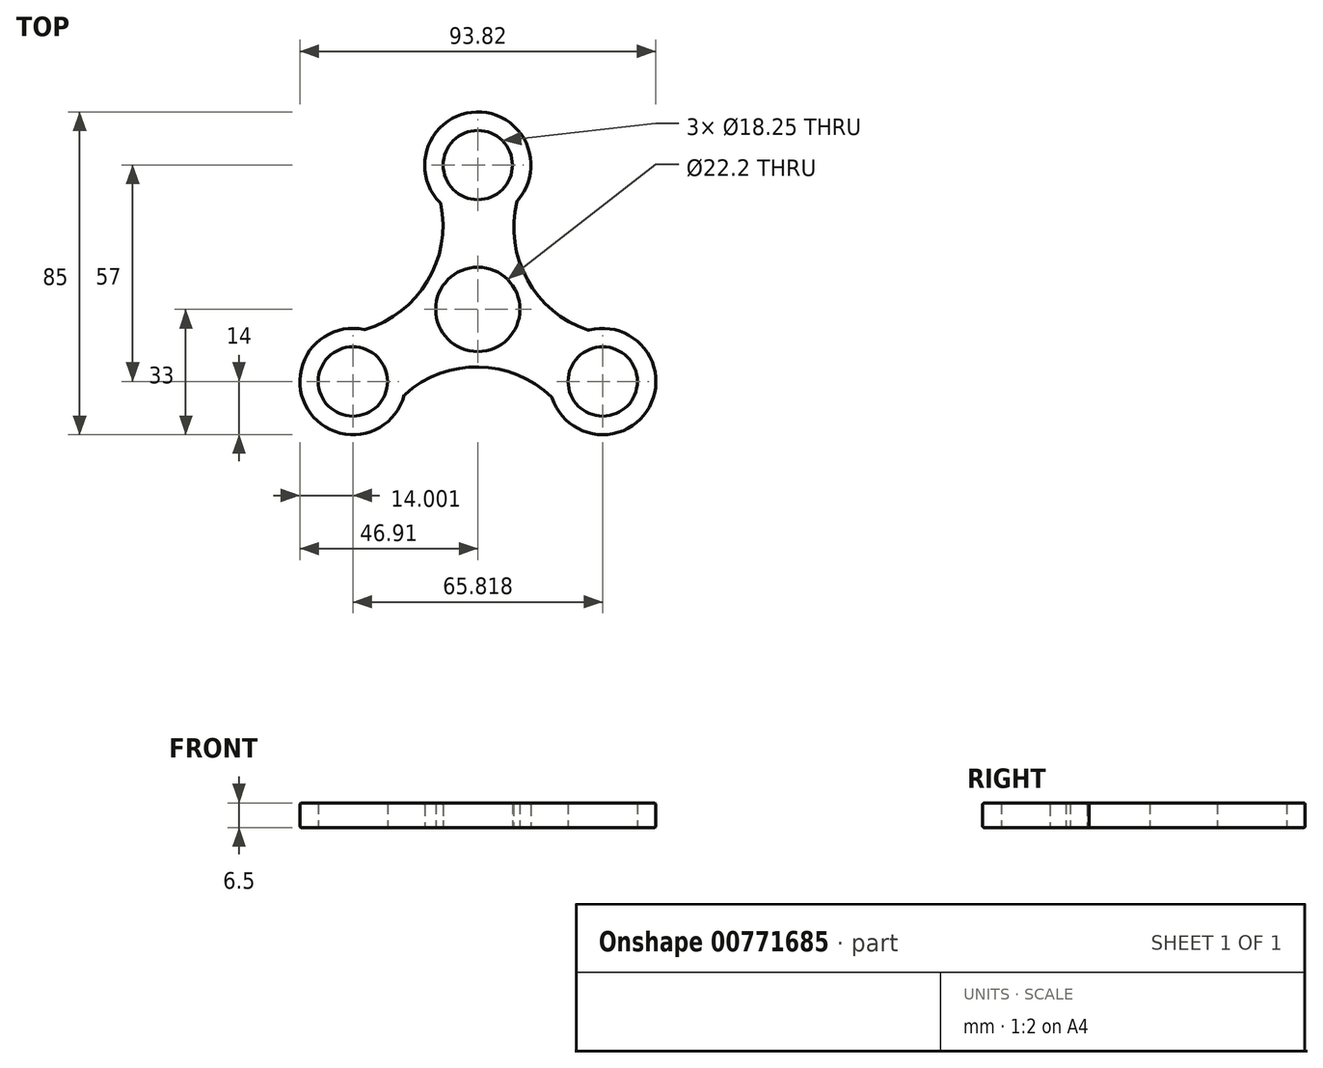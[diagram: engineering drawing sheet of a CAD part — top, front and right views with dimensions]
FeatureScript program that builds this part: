
annotation { "Feature Type Name" : "Feature", "Feature Type Description" : "" }
export const myFeature = defineFeature(function(context is Context, id is Id, definition is map)
    precondition{}
    {
        {
            var Q0;
            Q0=qCreatedBy(makeId("Top.planeOp"),FACE);
            var sketch = newSketch(context, id + "F0", { "sketchPlane" : qUnion([Q0])});
            skCircle(sketch, "E0", {"center": v(0, 0) * mm, "radius": 11.1 * mm});
            skCircle(sketch, "E1", {"center": v(0, 0) * mm, "radius": 14 * mm});
            skCircle(sketch, "E2", {"center": v(0, 38) * mm, "radius": 14 * mm});
            skCircle(sketch, "E3", {"center": v(0, 38) * mm, "radius": 9.12 * mm});
            skCircle(sketch, "E4.1.0", {"center": v(-32.9, -19) * mm, "radius": 9.12 * mm});
            skCircle(sketch, "E4.1.1", {"center": v(-32.9, -19) * mm, "radius": 14 * mm});
            skCircle(sketch, "E4.2.0", {"center": v(32.9, -19) * mm, "radius": 9.12 * mm});
            skCircle(sketch, "E4.2.1", {"center": v(32.9, -19) * mm, "radius": 14 * mm});
            skArc(sketch, "E5", {"start": v(-39.1, -6.44) * mm, "mid": v(-12.89, 8.06) * mm, "end": v(-14, 38) * mm});
            skArc(sketch, "E6.1.0", {"start": v(25.13, -30.64) * mm, "mid": v(-0.54, -15.2) * mm, "end": v(-25.9, -31.12) * mm});
            skArc(sketch, "E6.2.0", {"start": v(13.97, 37.08) * mm, "mid": v(13.43, 7.13) * mm, "end": v(39.9, -6.88) * mm});
            skSolve(sketch);
        }
        {
            var Q0;
            Q0 = qSketchRegion(id + "F0", true);
            var Q1;
            Q1=makeQuery(id+"F0.imprint","IMPRINT",FACE,{"disambiguationData":[TD([[makeQuery(id+"F0.imprint","IMPRINT",EDGE,{"derivedFrom":sQuery(id+"F0.wireOp",EDGE,"E0")}),-1.0]])]});
            extrude(context, id + "F1", {"entities" : qUnion([Q0, Q1]), "depth" : 6.5 * mm, "offsetDistance" : 25 * mm});
        }
        {
            var Q0;
            Q0=makeQuery(id+"F1.opExtrude","SWEPT_FACE",FACE,{"disambiguationData":[OSD([sQuery(id+"F0.wireOp",EDGE,"E6.1.0")])]});
            var Q1;
            Q1=makeQuery(id+"F1.opExtrude","SWEPT_FACE",FACE,{"disambiguationData":[OSD([sQuery(id+"F0.wireOp",EDGE,"E4.1.1")])]});
            var Q2;
            Q2=makeQuery(id+"F1.opExtrude","SWEPT_FACE",FACE,{"disambiguationData":[OSD([sQuery(id+"F0.wireOp",EDGE,"E4.2.1")])]});
            var Q3;
            Q3=makeQuery(id+"F1.opExtrude","SWEPT_FACE",FACE,{"disambiguationData":[OSD([sQuery(id+"F0.wireOp",EDGE,"E6.2.0")])]});
            var Q4;
            Q4=makeQuery(id+"F1.opExtrude","SWEPT_FACE",FACE,{"disambiguationData":[OSD([sQuery(id+"F0.wireOp",EDGE,"E2")])]});
            var Q5;
            Q5=makeQuery(id+"F1.opExtrude","SWEPT_FACE",FACE,{"disambiguationData":[OSD([sQuery(id+"F0.wireOp",EDGE,"E5")])]});
            fillet(context, id + "F2", {"entities" : qUnion([Q0, Q1, Q2, Q3, Q4, Q5]), "radius" : 0.5 * mm, "tangentPropagation" : true, "allowEdgeOverflow" : false});
        }
    });
